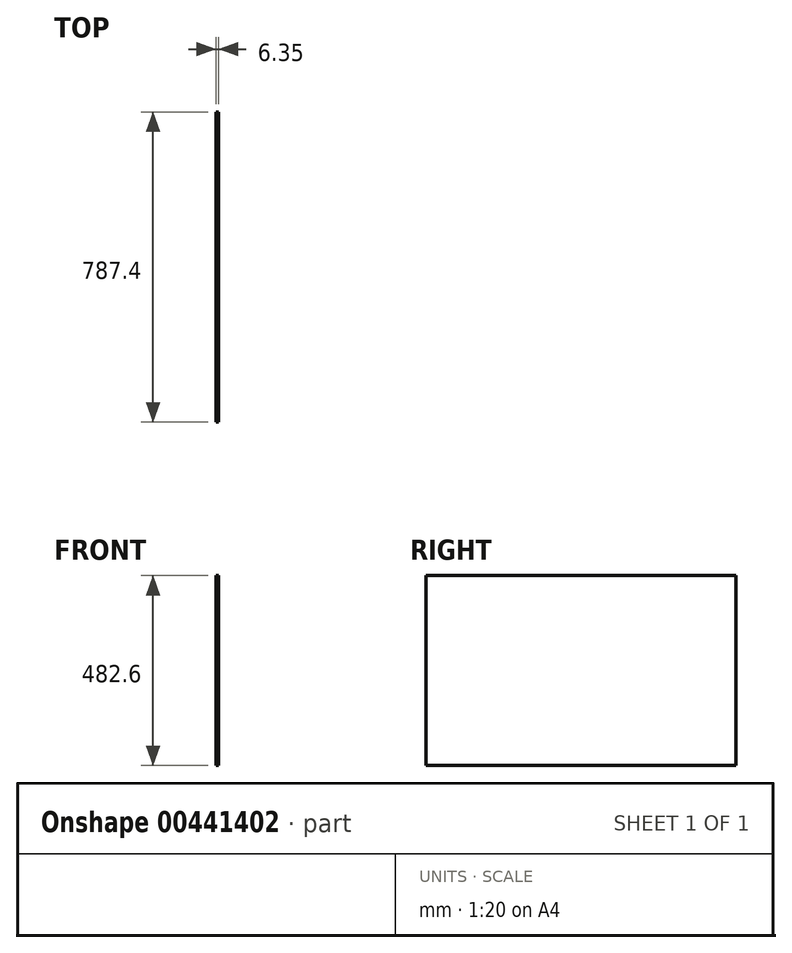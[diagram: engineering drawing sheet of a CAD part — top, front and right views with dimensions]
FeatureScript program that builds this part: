
annotation { "Feature Type Name" : "Feature", "Feature Type Description" : "" }
export const myFeature = defineFeature(function(context is Context, id is Id, definition is map)
    precondition{}
    {
        {
            var Q0;
            Q0=qCreatedBy(makeId("Right.planeOp"),FACE);
            var sketch = newSketch(context, id + "F0", { "sketchPlane" : qUnion([Q0])});
            skLineSegment(sketch, "E0.bottom", {"start": v(-393.7, 241.3) * mm, "end": v(393.7, 241.3) * mm});
            skLineSegment(sketch, "E0.top", {"start": v(-393.7, -241.3) * mm, "end": v(393.7, -241.3) * mm});
            skLineSegment(sketch, "E0.left", {"start": v(-393.7, 241.3) * mm, "end": v(-393.7, -241.3) * mm});
            skLineSegment(sketch, "E0.right", {"start": v(393.7, 241.3) * mm, "end": v(393.7, -241.3) * mm});
            skPoint(sketch, "E0.middle", {"position": v(0, 0) * mm});
            skSolve(sketch);
        }
        {
            var Q0;
            Q0 = qSketchRegion(id + "F0", true);
            extrude(context, id + "F1", {"entities" : qUnion([Q0]), "depth" : 6.35 * mm});
        }
    });
